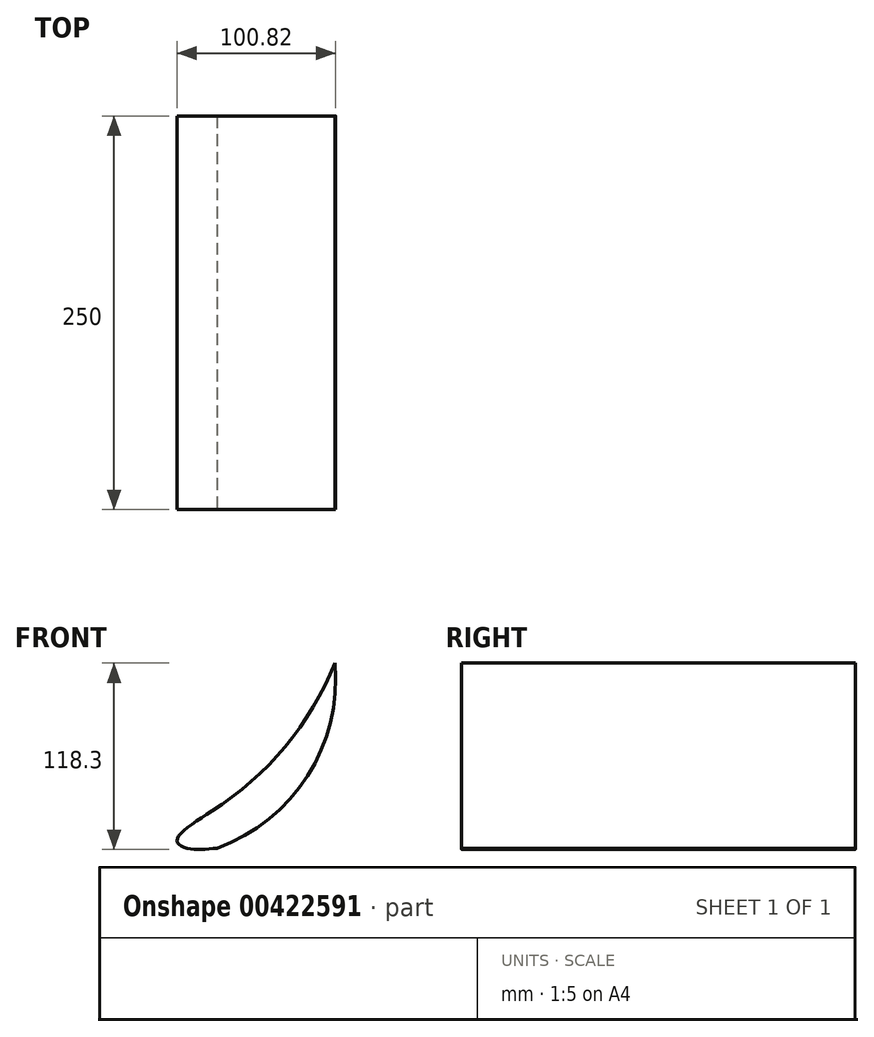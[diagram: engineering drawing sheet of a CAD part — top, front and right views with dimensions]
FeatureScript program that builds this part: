
annotation { "Feature Type Name" : "Feature", "Feature Type Description" : "" }
export const myFeature = defineFeature(function(context is Context, id is Id, definition is map)
    precondition{}
    {
        {
            var Q0;
            Q0=qCreatedBy(makeId("Front.planeOp"),FACE);
            cPlane(context, id + "F0", {"entities" : qUnion([Q0]), "cplaneType" : CPlaneType.OFFSET, "offset" : 253 * mm, "oppositeDirection" : true, "width" : 150 * mm, "height" : 150 * mm});
        }
        {
            var Q0;
            Q0=qCreatedBy(id+"F0.planeOp",FACE);
            var sketch = newSketch(context, id + "F1", { "sketchPlane" : qUnion([Q0])});
            skPoint(sketch, "E0", {"position": v(-847.8, 358.3) * mm});
            skPoint(sketch, "E1", {"position": v(-922.65, 240.76) * mm});
            skPoint(sketch, "E2", {"position": v(-941.58, 240.76) * mm});
            skPoint(sketch, "E3", {"position": v(-948.16, 245.77) * mm});
            skPoint(sketch, "E4", {"position": v(-925.87, 264.41) * mm});
            skFitSpline(sketch, "E5", {"points": [v(-922.65, 240.76) * mm, v(-941.58, 240.76) * mm, v(-948.16, 245.77) * mm, v(-925.87, 264.41) * mm], "startDerivative": vector(-58.61, -5.68) * mm, "endDerivative": vector(77.77, 49.45) * mm});
            skArc(sketch, "E6", {"start": v(-925.87, 264.41) * mm, "mid": v(-879.48, 305.25) * mm, "end": v(-847.8, 358.3) * mm});
            skArc(sketch, "E7", {"start": v(-922.65, 240.76) * mm, "mid": v(-865.21, 286.8) * mm, "end": v(-847.8, 358.3) * mm});
            skSolve(sketch);
        }
        {
            var Q0;
            Q0=makeQuery(id+"F1.imprint","IMPRINT",FACE,{"disambiguationData":[TD([[makeQuery(id+"F1.imprint","IMPRINT",EDGE,{"derivedFrom":sQuery(id+"F1.wireOp",EDGE,"E5")}),-1.0]])]});
            extrude(context, id + "F2", {"entities" : qUnion([Q0]), "oppositeDirection" : true, "depth" : 250 * mm});
        }
    });
